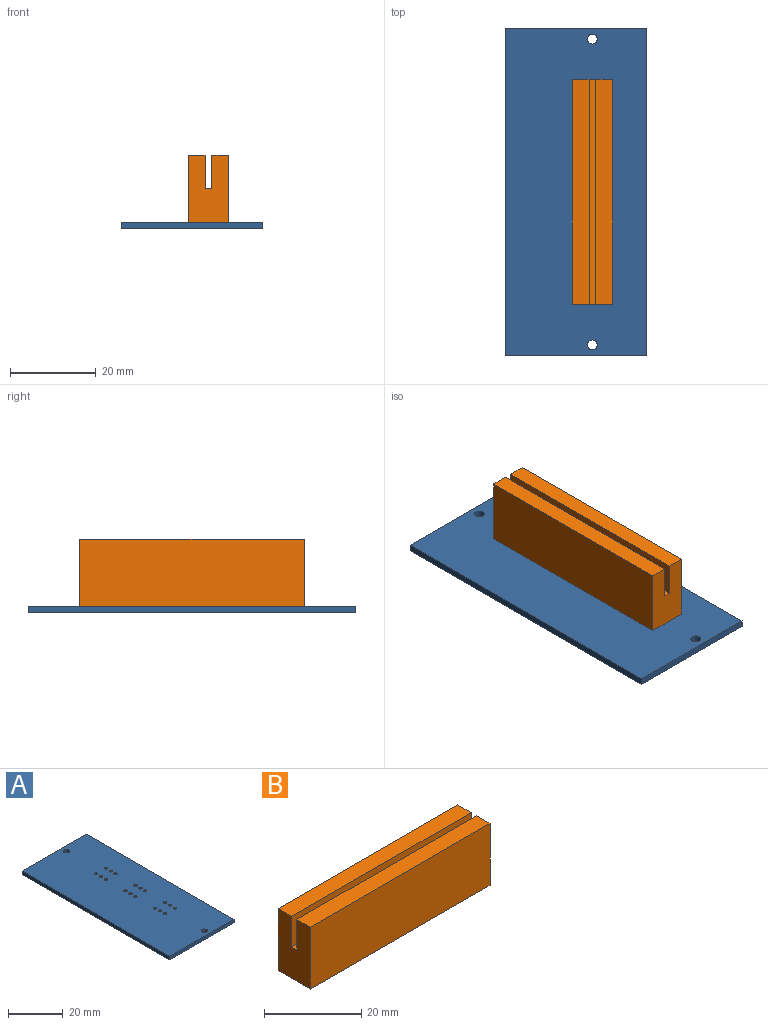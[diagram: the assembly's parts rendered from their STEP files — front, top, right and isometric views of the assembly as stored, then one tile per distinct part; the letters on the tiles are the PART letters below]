
ASSEMBLY  parts=2 mates=1
PART A: 26 faces, bbox 33x76.2x1.6 mm
  f0: plane 33.02x1.6mm, normal (0,-1,0), area 52.8mm2, adj f1,f23,f24,f25
  f1: plane 76.2x1.6mm, normal (1,0,0), area 121.9mm2, adj f0,f2,f24,f25
  f2: plane 33.02x1.6mm, normal (0,1,0), area 52.8mm2, adj f1,f23,f24,f25
  f3: cylinder r=1.14mm len=2.29mm, axis (0,0,-1), area 11.5mm2, adj f24,f25
  f4: cylinder r=1.14mm len=2.29mm, axis (0,0,-1), area 11.5mm2, adj f24,f25
  f5: cylinder r=0.64mm len=1.6mm, axis (0,0,-1), area 6.4mm2, adj f24,f25
  f6: cylinder r=0.64mm len=1.6mm, axis (0,0,-1), area 6.4mm2, adj f24,f25
  f7: cylinder r=0.64mm len=1.6mm, axis (0,0,-1), area 6.4mm2, adj f24,f25
  f8: cylinder r=0.64mm len=1.6mm, axis (0,0,-1), area 6.4mm2, adj f24,f25
  f9: cylinder r=0.64mm len=1.6mm, axis (0,0,-1), area 6.4mm2, adj f24,f25
  f10: cylinder r=0.64mm len=1.6mm, axis (0,0,-1), area 6.4mm2, adj f24,f25
  f11: cylinder r=0.64mm len=1.6mm, axis (0,0,-1), area 6.4mm2, adj f24,f25
  f12: cylinder r=0.64mm len=1.6mm, axis (0,0,-1), area 6.4mm2, adj f24,f25
  f13: cylinder r=0.64mm len=1.6mm, axis (0,0,-1), area 6.4mm2, adj f24,f25
  f14: cylinder r=0.64mm len=1.6mm, axis (0,0,-1), area 6.4mm2, adj f24,f25
  f15: cylinder r=0.64mm len=1.6mm, axis (0,0,-1), area 6.4mm2, adj f24,f25
  f16: cylinder r=0.64mm len=1.6mm, axis (0,0,-1), area 6.4mm2, adj f24,f25
  f17: cylinder r=0.64mm len=1.6mm, axis (0,0,-1), area 6.4mm2, adj f24,f25
  f18: cylinder r=0.64mm len=1.6mm, axis (0,0,-1), area 6.4mm2, adj f24,f25
  f19: cylinder r=0.64mm len=1.6mm, axis (0,0,-1), area 6.4mm2, adj f24,f25
  f20: cylinder r=0.64mm len=1.6mm, axis (0,0,-1), area 6.4mm2, adj f24,f25
  f21: cylinder r=0.64mm len=1.6mm, axis (0,0,-1), area 6.4mm2, adj f24,f25
  f22: cylinder r=0.64mm len=1.6mm, axis (0,0,-1), area 6.4mm2, adj f24,f25
  f23: plane 76.2x1.6mm, normal (-1,0,0), area 121.9mm2, adj f0,f2,f24,f25
  f24: plane 76.2x33.02mm, normal (0,0,1), area 2485.1mm2, adj f0,f1,f2,f3,f4,f5,f6,f7
  f25: plane 76.2x33.02mm, normal (0,0,-1), area 2485.1mm2, adj f0,f1,f2,f3,f4,f5,f6,f7
PART B: 10 faces, bbox 52.3x9.4x15.6 mm
  f0: plane 52.32x3.92mm, normal (0,0,1), area 205.3mm2, adj f1,f2,f3,f7
  f1: plane 15.6x9.4mm, normal (1,0,0), area 134.7mm2, adj f0,f2,f4,f5,f6,f7,f8,f9
  f2: plane 52.32x15.6mm, normal (0,1,0), area 816.3mm2, adj f0,f1,f3,f6
  f3: plane 15.6x9.4mm, normal (-1,0,0), area 134.7mm2, adj f0,f2,f4,f5,f6,f7,f8,f9
  f4: plane 52.32x15.6mm, normal (0,-1,0), area 816.3mm2, adj f1,f3,f5,f6
  f5: plane 52.32x3.92mm, normal (0,0,1), area 205.3mm2, adj f1,f3,f4,f8
  f6: plane 52.32x9.4mm, normal (0,0,-1), area 491.7mm2, adj f1,f2,f3,f4
  f7: plane 52.32x7.7mm, normal (0,-1,0), area 402.9mm2, adj f0,f1,f3,f9
  f8: plane 52.32x7.7mm, normal (0,1,0), area 402.9mm2, adj f1,f3,f5,f9
  f9: plane 52.32x1.55mm, normal (0,0,1), area 81.1mm2, adj f1,f3,f7,f8
PLACE A t=(53.73,30.54,-0.8)mm
PLACE B rot(axis=(0,0,-1),90deg) t=(36.33,42.48,0.8)mm
MATE fastened B.f6 <-> A.f24  axis (0,0,-1) through (41.03,68.64,0.8)mm
